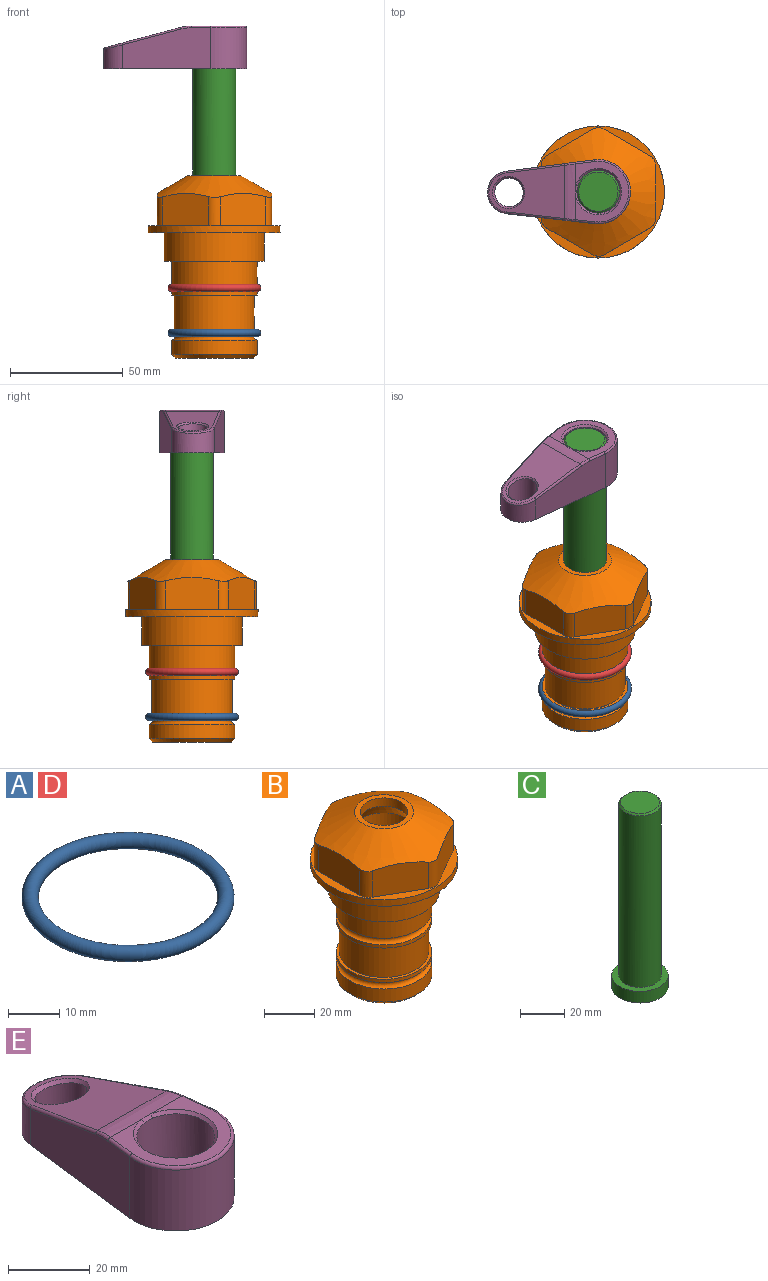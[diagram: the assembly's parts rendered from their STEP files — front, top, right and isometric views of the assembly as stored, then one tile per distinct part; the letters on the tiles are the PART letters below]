
ASSEMBLY  parts=5 mates=4
PART A: 1 faces, bbox 44.7x44.7x3.2 mm
  f0: torus R=19.05mm, axis (0,0,1), area 1193.9mm2
PART B: 36 faces, bbox 58.7x58.7x81 mm
  f0: cylinder r=17.78mm len=35.56mm, axis (0,0,1), area 1670.8mm2, adj f23,f24,f31
  f1: cylinder r=19.05mm len=38.1mm, axis (0,0,1), area 1191.9mm2, adj f26,f27,f30
  f2: plane 58.66x58.66mm, normal (0,0,-1), area 1150.6mm2, adj f3,f28
  f3: cylinder r=29.33mm len=58.66mm, axis (0,0,-1), area 585.1mm2, adj f2,f4
  f4: plane 58.66x58.66mm, normal (0,0,1), area 475.9mm2, adj f3,f5,f6,f7,f8,f9,f10,f11
  f5: plane 20.32x14.34mm, normal (-0.5,0.87,0), area 324.4mm2, adj f4,f15,f16,f17
  f6: plane 20.32x14.34mm, normal (0.5,0.87,0), area 324.4mm2, adj f4,f14,f15,f17
  f7: plane 23.48x14.34mm, normal (1,0,0), area 324.4mm2, adj f4,f13,f14,f17
  f8: plane 20.32x14.34mm, normal (0.5,-0.87,0), area 324.4mm2, adj f4,f12,f13,f17
  f9: plane 20.32x14.34mm, normal (-0.5,-0.87,0), area 324.4mm2, adj f4,f11,f12,f17
  f10: plane 23.48x14.34mm, normal (-1,0,0), area 324.4mm2, adj f4,f11,f16,f17
  f11: cylinder r=5.08mm len=12.85mm, axis (0,0,-1), area 67.2mm2, adj f4,f9,f10,f17
  f12: cylinder r=5.08mm len=12.85mm, axis (0,0,-1), area 67.2mm2, adj f4,f8,f9,f17
  f13: cylinder r=5.08mm len=12.85mm, axis (0,0,-1), area 67.2mm2, adj f4,f7,f8,f17
  f14: cylinder r=5.08mm len=12.85mm, axis (0,0,-1), area 67.2mm2, adj f4,f6,f7,f17
  f15: cylinder r=5.08mm len=12.85mm, axis (0,0,-1), area 67.2mm2, adj f4,f5,f6,f17
  f16: cylinder r=5.08mm len=12.85mm, axis (0,0,-1), area 67.2mm2, adj f4,f5,f10,f17
  f17: cone r=11.73mm half-angle=60deg, axis (0,0,-1), area 2071.8mm2, adj f5,f6,f7,f8,f9,f10,f11,f12
  f18: plane 23.46x23.46mm, normal (0,0,1), area 147.4mm2, adj f17,f35
  f19: plane 34.93x34.93mm, normal (0,0,-1), area 958mm2, adj f29
  f20: cylinder r=19.05mm len=38.1mm, axis (0,0,1), area 760.1mm2, adj f21,f29
  f21: torus R=19.05mm, axis (0,0,1), area 565.3mm2, adj f20,f22
  f22: cylinder r=19.05mm len=38.1mm, axis (0,0,1), area 190mm2, adj f21,f23
  f23: plane 38.1x38.1mm, normal (0,0,1), area 146.9mm2, adj f0,f22
  f24: plane 38.1x38.1mm, normal (0,0,-1), area 146.9mm2, adj f0,f25
  f25: cylinder r=19.05mm len=38.1mm, axis (0,0,1), area 190mm2, adj f24,f26
  f26: torus R=19.05mm, axis (0,0,1), area 565.3mm2, adj f1,f25
  f27: plane 44.45x44.45mm, normal (0,0,-1), area 411.7mm2, adj f1,f28
  f28: cylinder r=22.23mm len=44.45mm, axis (0,0,1), area 1773.5mm2, adj f2,f27
  f29: cone r=19.05mm half-angle=45deg, axis (0,0,1), area 257.5mm2, adj f19,f20
  f30: cylinder r=3.17mm len=6.75mm, axis (-1,0,0), area 128mm2, adj f1,f33
  f31: cylinder r=3.17mm len=6.35mm, axis (-1,0,0), area 102.5mm2, adj f0,f33
  f32: plane 25.4x25.4mm, normal (0,0,1), area 506.7mm2, adj f33
  f33: cylinder r=12.7mm len=66.42mm, axis (0,0,-1), area 5236.2mm2, adj f30,f31,f32,f34
  f34: cone r=9.53mm half-angle=30deg, axis (0,0,-1), area 443.4mm2, adj f33,f35
  f35: cylinder r=9.53mm len=19.05mm, axis (0,0,-1), area 240.9mm2, adj f18,f34
PART C: 6 faces, bbox 25.4x25.4x101.6 mm
  f0: plane 17.46x17.46mm, normal (0,0,1), area 239.5mm2, adj f5
  f1: plane 25.4x25.4mm, normal (0,0,-1), area 506.7mm2, adj f2
  f2: cylinder r=12.7mm len=25.4mm, axis (0,0,1), area 506.7mm2, adj f1,f3
  f3: plane 25.4x25.4mm, normal (0,0,1), area 221.7mm2, adj f2,f4
  f4: cylinder r=9.53mm len=94.46mm, axis (0,0,1), area 5653mm2, adj f3,f5
  f5: cone r=8.73mm half-angle=45deg, axis (0,0,-1), area 64.4mm2, adj f0,f4
PART D: same geometry as A
PART E: 31 faces, bbox 31.7x65.5x19.8 mm
  f0: plane 39.12x18.26mm, normal (0.99,0.12,0), area 612.2mm2, adj f1,f4,f7,f11,f13,f15
  f1: cylinder r=9.53mm len=18.91mm, axis (0,0,-1), area 296.1mm2, adj f0,f2,f7,f17
  f2: plane 39.12x18.26mm, normal (-0.99,0.12,0), area 612.2mm2, adj f1,f4,f7,f12,f14,f16
  f3: cylinder r=6.35mm len=12.7mm, axis (0,0,-1), area 362.4mm2, adj f7,f18
  f4: cylinder r=14.29mm len=28.58mm, axis (0,0,-1), area 882.2mm2, adj f0,f2,f7,f10
  f5: cylinder r=9.53mm len=19.05mm, axis (0,0,-1), area 1092.6mm2, adj f7,f19,f20
  f6: plane 26.99x23.69mm, normal (0,0,1), area 216.2mm2, adj f9,f10,f11,f12,f19
  f7: plane 63.5x28.58mm, normal (0,0,-1), area 661.8mm2, adj f0,f1,f2,f3,f4,f5,f22,f23
  f8: plane 33.52x23.6mm, normal (0,0.26,0.97), area 486mm2, adj f9,f15,f16,f17,f18
  f9: cylinder r=19.05mm len=24.72mm, axis (1,0,0), area 120.4mm2, adj f6,f8,f13,f14,f20
  f10: torus R=13.49mm, axis (0,0,1), area 59mm2, adj f4,f6,f11,f12
  f11: cylinder r=0.79mm len=8.67mm, axis (0.12,-0.99,0), area 10.8mm2, adj f0,f6,f10,f13
  f12: cylinder r=0.79mm len=8.67mm, axis (0.12,0.99,0), area 10.8mm2, adj f2,f6,f10,f14
  f13: bspline ~4.95x1.42mm, area 6.1mm2, adj f0,f9,f11,f15
  f14: bspline ~4.95x1.42mm, area 6.1mm2, adj f2,f9,f12,f16
  f15: cylinder r=0.79mm len=25.95mm, axis (0.12,-0.96,0.26), area 32.9mm2, adj f0,f8,f13,f17
  f16: cylinder r=0.79mm len=25.95mm, axis (0.12,0.96,-0.26), area 32.9mm2, adj f2,f8,f14,f17
  f17: bspline ~18.91x8.38mm, area 30mm2, adj f1,f8,f15,f16
  f18: bspline ~14.29x14.29mm, area 48.3mm2, adj f3,f8
  f19: cone r=9.53mm half-angle=45deg, axis (0,0,1), area 66.5mm2, adj f5,f6,f20
  f20: bspline ~3.22x0.96mm, area 3.5mm2, adj f5,f9,f19
  f21: plane 2.75x2.72mm, normal (0,0,-1), area 2.9mm2, adj f23,f25,f28
  f22: plane 23.05x15.88mm, normal (-0.99,-0.12,0), area 323.6mm2, adj f7,f25,f26,f27,f28,f29
  f23: plane 23.05x15.88mm, normal (0.99,-0.12,0), area 323.6mm2, adj f7,f21,f25,f27,f28,f30
  f24: cylinder r=9.53mm len=10.69mm, axis (0,0,-1), area 114.7mm2, adj f7,f27,f29,f30
  f25: cylinder r=12.7mm len=20.59mm, axis (0,0,-1), area 381.1mm2, adj f7,f21,f22,f23,f26,f28
  f26: plane 2.75x2.72mm, normal (0,0,-1), area 2.9mm2, adj f22,f25,f28
  f27: plane 19.72x18.37mm, normal (0,-0.26,-0.97), area 291.8mm2, adj f22,f23,f24,f28,f29,f30
  f28: cylinder r=15.88mm len=19.92mm, axis (1,0,0), area 54.8mm2, adj f21,f22,f23,f25,f26,f27
  f29: cylinder r=1.59mm len=11mm, axis (0,0,-1), area 34.7mm2, adj f7,f22,f24,f27
  f30: cylinder r=1.59mm len=11mm, axis (0,0,-1), area 34.7mm2, adj f7,f23,f24,f27
PLACE A t=(0,0,-20)mm
PLACE B at identity fixed
PLACE C rot(axis=(0,0,1),90.5deg) t=(0,0,27.55)mm
PLACE D at identity
PLACE E rot(axis=(0,0,1),90.5deg) t=(0,0,28.35)mm
MATE fastened D.f0 <-> B.f0  axis (0,0,1) through (0,0,-24.51)mm
MATE fastened C.f2 <-> E.f4  axis (0,0,1) through (0,0,91.05)mm
MATE fastened A.f0 <-> B.f0  axis (0,0,1) through (0,0,-44.51)mm
MATE cylindrical B.f0 <-> C.f2  axis (0,0,1) through (0,0,-50.55)mm
